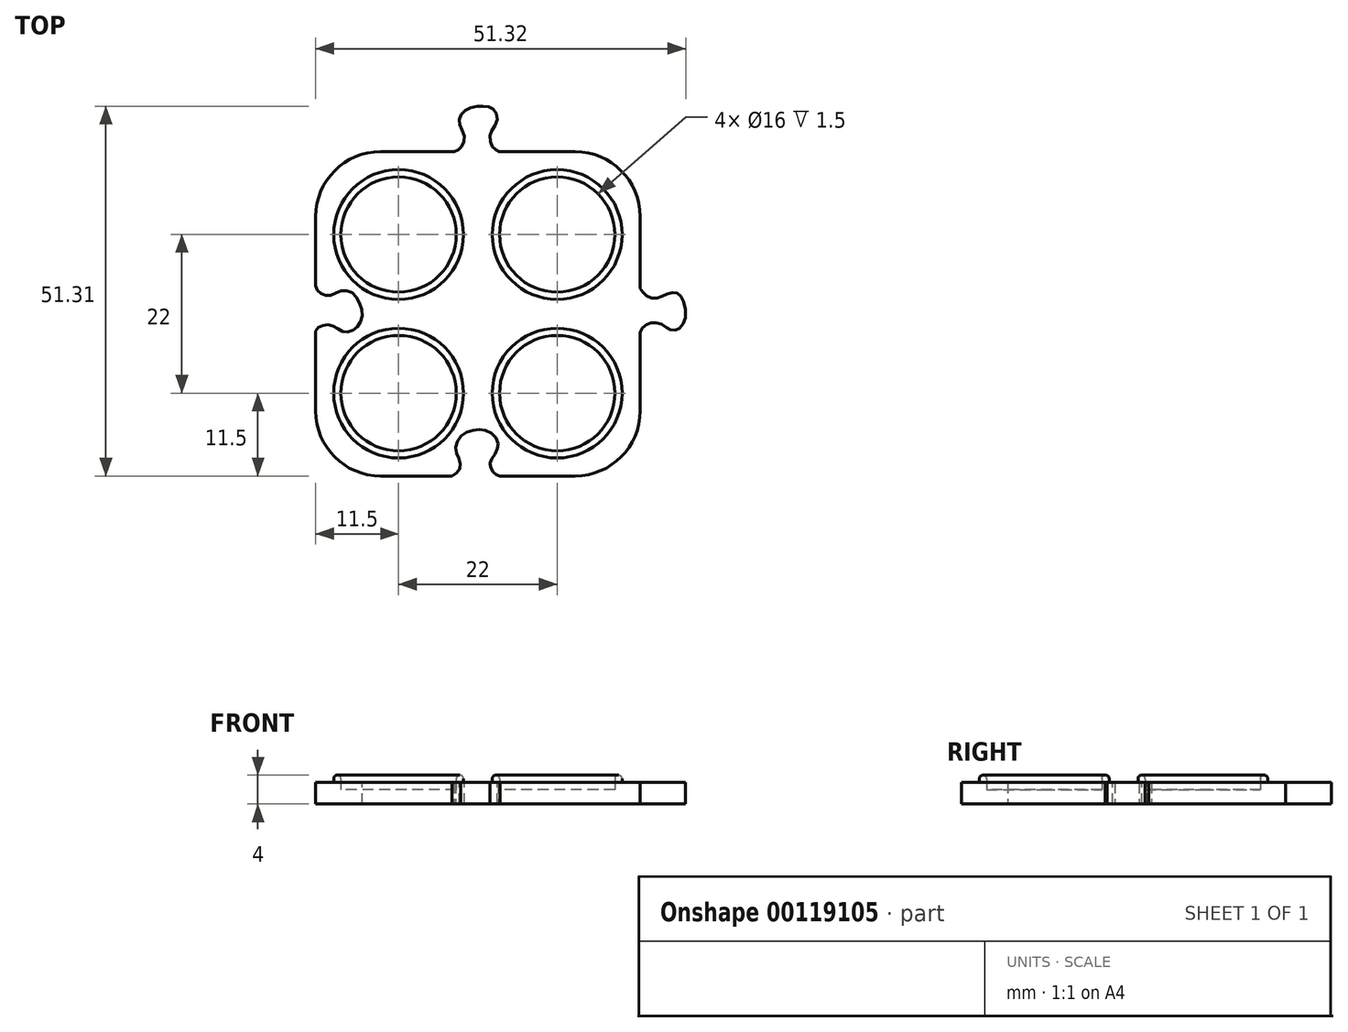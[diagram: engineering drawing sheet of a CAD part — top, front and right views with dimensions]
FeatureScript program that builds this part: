
annotation { "Feature Type Name" : "Feature", "Feature Type Description" : "" }
export const myFeature = defineFeature(function(context is Context, id is Id, definition is map)
    precondition{}
    {
        {
            var Q0;
            Q0=qCreatedBy(makeId("Top.planeOp"),FACE);
            var sketch = newSketch(context, id + "F0", { "sketchPlane" : qUnion([Q0])});
            skLineSegment(sketch, "E0.bottom", {"start": v(13.5, 13.5) * mm, "end": v(2.93, 13.5) * mm});
            skLineSegment(sketch, "E0.top", {"start": v(13.5, -13.5) * mm, "end": v(3.04, -13.5) * mm});
            skLineSegment(sketch, "E0.left", {"start": v(13.5, 13.5) * mm, "end": v(13.5, 3.49) * mm});
            skLineSegment(sketch, "E0.right", {"start": v(-13.5, 13.5) * mm, "end": v(-13.5, 3.89) * mm});
            skPoint(sketch, "E0.middle", {"position": v(0, 0) * mm});
            skFitSpline(sketch, "E1", {"points": [v(-13.5, -2.4) * mm, v(-13.06, -1.85) * mm, v(-12.19, -1.54) * mm, v(-11.23, -1.64) * mm, v(-10.18, -2.22) * mm, v(-9.3, -2.53) * mm, v(-8.23, -2.22) * mm, v(-7.52, -1.5) * mm, v(-7.03, -0.16) * mm, v(-7.37, 1.42) * mm, v(-8.21, 2.75) * mm, v(-9.3, 3.24) * mm, v(-10.53, 3) * mm, v(-11.5, 2.56) * mm, v(-12.42, 2.62) * mm, v(-13.18, 3.16) * mm, v(-13.5, 3.89) * mm], "startDerivative": vector(7.23, 11.93) * mm, "endDerivative": vector(-4.43, 14.21) * mm});
            skFitSpline(sketch, "E2", {"points": [v(-3.62, -13.5) * mm, v(-2.74, -12.9) * mm, v(-2.4, -12.05) * mm, v(-2.66, -11.08) * mm, v(-3.04, -10.02) * mm, v(-2.9, -8.8) * mm, v(-1.99, -7.67) * mm, v(-0.58, -7.14) * mm, v(0.76, -7.1) * mm, v(1.96, -7.62) * mm, v(2.79, -8.82) * mm, v(2.7, -9.8) * mm, v(2.12, -10.8) * mm, v(1.7, -11.65) * mm, v(1.76, -12.32) * mm, v(2.16, -13.02) * mm, v(2.6, -13.36) * mm, v(3.04, -13.5) * mm], "startDerivative": vector(16.2, 8.74) * mm, "endDerivative": vector(11.53, -2.8) * mm});
            skFitSpline(sketch, "E3", {"points": [v(-3.26, 13.5) * mm, v(-2.68, 13.76) * mm, v(-2.1, 14.46) * mm, v(-1.88, 15.61) * mm, v(-2.4, 17) * mm, v(-2.57, 17.9) * mm, v(-2.1, 18.93) * mm, v(-0.95, 19.6) * mm, v(0.43, 19.8) * mm, v(1.54, 19.7) * mm, v(2.37, 19.12) * mm, v(2.65, 17.8) * mm, v(2.02, 16.6) * mm, v(1.68, 15.55) * mm, v(1.92, 14.36) * mm, v(2.47, 13.75) * mm, v(2.93, 13.5) * mm], "startDerivative": vector(12.36, 4.01) * mm, "endDerivative": vector(10.48, -4.73) * mm});
            skFitSpline(sketch, "E4", {"points": [v(13.5, -2.57) * mm, v(13.97, -1.82) * mm, v(14.8, -1.34) * mm, v(15.69, -1.25) * mm, v(16.88, -1.66) * mm, v(17.63, -2.18) * mm, v(18.47, -2.24) * mm, v(19.2, -1.75) * mm, v(19.8, -0.34) * mm, v(19.4, 1.93) * mm, v(18.82, 2.75) * mm, v(18.04, 2.97) * mm, v(16.92, 2.58) * mm, v(15.97, 2.23) * mm, v(14.85, 2.24) * mm, v(13.98, 2.93) * mm, v(13.5, 3.49) * mm], "startDerivative": vector(6.76, 14.24) * mm, "endDerivative": vector(-8.43, 10.21) * mm});
            skLineSegment(sketch, "E5.trimOffspring", {"start": v(-3.26, 13.5) * mm, "end": v(-13.5, 13.5) * mm});
            skLineSegment(sketch, "E6.trimOffspring", {"start": v(13.5, -2.57) * mm, "end": v(13.5, -13.5) * mm});
            skLineSegment(sketch, "E7.trimOffspring", {"start": v(-3.62, -13.5) * mm, "end": v(-13.5, -13.5) * mm});
            skLineSegment(sketch, "E8.trimOffspring", {"start": v(-13.5, -2.4) * mm, "end": v(-13.5, -13.5) * mm});
            skPoint(sketch, "E9.visualSharp", {"position": v(-13.5, 13.5) * mm});
            skLineSegment(sketch, "E9.filletArc", {"start": v(-13.5, 13.5) * mm, "end": v(-13.5, 13.5) * mm});
            skPoint(sketch, "E10.visualSharp", {"position": v(13.5, 13.5) * mm});
            skLineSegment(sketch, "E10.filletArc", {"start": v(13.5, 13.5) * mm, "end": v(13.5, 13.5) * mm});
            skPoint(sketch, "E11.visualSharp", {"position": v(13.5, -13.5) * mm});
            skLineSegment(sketch, "E11.filletArc", {"start": v(13.5, -13.5) * mm, "end": v(13.5, -13.5) * mm});
            skPoint(sketch, "E12.visualSharp", {"position": v(-13.5, -13.5) * mm});
            skLineSegment(sketch, "E12.filletArc", {"start": v(-13.5, -13.5) * mm, "end": v(-13.5, -13.5) * mm});
            skLineSegment(sketch, "E13", {"start": v(-13.5, 4.5) * mm, "end": v(13.5, 4.5) * mm});
            skLineSegment(sketch, "E14", {"start": v(-4.5, 13.5) * mm, "end": v(-4.5, -13.5) * mm});
            skLineSegment(sketch, "E15", {"start": v(-13.5, -4.5) * mm, "end": v(13.5, -4.5) * mm});
            skLineSegment(sketch, "E16", {"start": v(4.5, 13.5) * mm, "end": v(4.5, -13.5) * mm});
            skSolve(sketch);
        }
        {
            var Q0;
            {var subQ1=sQuery(id+"F0.wireOp",EDGE,"E3");Q0=makeQuery(id+"F0.imprint","IMPRINT",FACE,{"disambiguationData":[TD([[makeQuery(id+"F0.imprint","IMPRINT",EDGE,{"derivedFrom":subQ1}),-1.0]])]});}
            var Q1;
            {var subQ0=sQuery(id+"F0.wireOp",EDGE,"E5.trimOffspring");var subQ1=sQuery(id+"F0.wireOp",EDGE,"E0.right");var subQ2=makeQuery(id+"F0.imprint","INTERSECT",VERTEX,{"derivedFrom":[subQ1,subQ0]});Q1=makeQuery(id+"F0.imprint","IMPRINT",FACE,{"disambiguationData":[TD([[makeQuery(id+"F0.imprint","IMPRINT",EDGE,{"disambiguationData":[TD([[subQ2,-1.0]])],"derivedFrom":subQ1}),1.0]])]});}
            var Q2;
            {var subQ0=sQuery(id+"F0.wireOp",EDGE,"E0.left");var subQ1=sQuery(id+"F0.wireOp",EDGE,"E0.bottom");var subQ2=makeQuery(id+"F0.imprint","INTERSECT",VERTEX,{"derivedFrom":[subQ1,subQ0]});Q2=makeQuery(id+"F0.imprint","IMPRINT",FACE,{"disambiguationData":[TD([[makeQuery(id+"F0.imprint","IMPRINT",EDGE,{"disambiguationData":[TD([[subQ2,-1.0]])],"derivedFrom":subQ1}),1.0]])]});}
            var Q3;
            {var subQ0=sQuery(id+"F0.wireOp",EDGE,"E14");var subQ1=sQuery(id+"F0.wireOp",EDGE,"E13");var subQ2=makeQuery(id+"F0.imprint","INTERSECT",VERTEX,{"derivedFrom":[subQ1,subQ0]});Q3=makeQuery(id+"F0.imprint","IMPRINT",FACE,{"disambiguationData":[TD([[makeQuery(id+"F0.imprint","IMPRINT",EDGE,{"disambiguationData":[TD([[subQ2,-1.0]])],"derivedFrom":subQ1}),-1.0]])]});}
            extrude(context, id + "F1", {"entities" : qUnion([Q0, Q1, Q2, Q3]), "depth" : 3 * mm});
        }
        {
            var Q0;
            {var subQ5=sQuery(id+"F0.wireOp",EDGE,"E4");Q0=makeQuery(id+"F0.imprint","IMPRINT",FACE,{"disambiguationData":[TD([[makeQuery(id+"F0.imprint","IMPRINT",EDGE,{"derivedFrom":subQ5}),1.0]])]});}
            var Q1;
            {var subQ0=sQuery(id+"F0.wireOp",EDGE,"E0.left");var subQ1=sQuery(id+"F0.wireOp",EDGE,"E0.bottom");var subQ2=makeQuery(id+"F0.imprint","INTERSECT",VERTEX,{"derivedFrom":[subQ1,subQ0]});Q1=makeQuery(id+"F0.imprint","IMPRINT",FACE,{"disambiguationData":[TD([[makeQuery(id+"F0.imprint","IMPRINT",EDGE,{"disambiguationData":[TD([[subQ2,-1.0]])],"derivedFrom":subQ1}),1.0]])]});}
            var Q2;
            {var subQ0=sQuery(id+"F0.wireOp",EDGE,"E6.trimOffspring");var subQ1=sQuery(id+"F0.wireOp",EDGE,"E0.top");var subQ2=makeQuery(id+"F0.imprint","INTERSECT",VERTEX,{"derivedFrom":[subQ1,subQ0]});Q2=makeQuery(id+"F0.imprint","IMPRINT",FACE,{"disambiguationData":[TD([[makeQuery(id+"F0.imprint","IMPRINT",EDGE,{"disambiguationData":[TD([[subQ2,-1.0]])],"derivedFrom":subQ1}),-1.0]])]});}
            var Q3;
            {var subQ0=sQuery(id+"F0.wireOp",EDGE,"E14");var subQ1=sQuery(id+"F0.wireOp",EDGE,"E13");var subQ2=makeQuery(id+"F0.imprint","INTERSECT",VERTEX,{"derivedFrom":[subQ1,subQ0]});Q3=makeQuery(id+"F0.imprint","IMPRINT",FACE,{"disambiguationData":[TD([[makeQuery(id+"F0.imprint","IMPRINT",EDGE,{"disambiguationData":[TD([[subQ2,-1.0]])],"derivedFrom":subQ1}),-1.0]])]});}
            extrude(context, id + "F2", {"entities" : qUnion([Q0, Q1, Q2, Q3]), "depth" : 3 * mm});
        }
        {
            var Q0;
            {var subQ5=sQuery(id+"F0.wireOp",EDGE,"E2");Q0=makeQuery(id+"F0.imprint","IMPRINT",FACE,{"disambiguationData":[TD([[makeQuery(id+"F0.imprint","IMPRINT",EDGE,{"derivedFrom":subQ5}),1.0]])]});}
            var Q1;
            {var subQ0=sQuery(id+"F0.wireOp",EDGE,"E8.trimOffspring");var subQ1=sQuery(id+"F0.wireOp",EDGE,"E7.trimOffspring");var subQ2=makeQuery(id+"F0.imprint","INTERSECT",VERTEX,{"derivedFrom":[subQ1,subQ0]});Q1=makeQuery(id+"F0.imprint","IMPRINT",FACE,{"disambiguationData":[TD([[makeQuery(id+"F0.imprint","IMPRINT",EDGE,{"disambiguationData":[TD([[subQ2,1.0]])],"derivedFrom":subQ1}),-1.0]])]});}
            var Q2;
            {var subQ0=sQuery(id+"F0.wireOp",EDGE,"E6.trimOffspring");var subQ1=sQuery(id+"F0.wireOp",EDGE,"E0.top");var subQ2=makeQuery(id+"F0.imprint","INTERSECT",VERTEX,{"derivedFrom":[subQ1,subQ0]});Q2=makeQuery(id+"F0.imprint","IMPRINT",FACE,{"disambiguationData":[TD([[makeQuery(id+"F0.imprint","IMPRINT",EDGE,{"disambiguationData":[TD([[subQ2,-1.0]])],"derivedFrom":subQ1}),-1.0]])]});}
            var Q3;
            {var subQ0=sQuery(id+"F0.wireOp",EDGE,"E14");var subQ1=sQuery(id+"F0.wireOp",EDGE,"E13");var subQ2=makeQuery(id+"F0.imprint","INTERSECT",VERTEX,{"derivedFrom":[subQ1,subQ0]});Q3=makeQuery(id+"F0.imprint","IMPRINT",FACE,{"disambiguationData":[TD([[makeQuery(id+"F0.imprint","IMPRINT",EDGE,{"disambiguationData":[TD([[subQ2,-1.0]])],"derivedFrom":subQ1}),-1.0]])]});}
            extrude(context, id + "F3", {"entities" : qUnion([Q0, Q1, Q2, Q3]), "depth" : 3 * mm});
        }
        {
            var Q0;
            {var subQ6=sQuery(id+"F0.wireOp",EDGE,"E1");Q0=makeQuery(id+"F0.imprint","IMPRINT",FACE,{"disambiguationData":[TD([[makeQuery(id+"F0.imprint","IMPRINT",EDGE,{"derivedFrom":subQ6}),-1.0]])]});}
            var Q1;
            {var subQ0=sQuery(id+"F0.wireOp",EDGE,"E5.trimOffspring");var subQ1=sQuery(id+"F0.wireOp",EDGE,"E0.right");var subQ2=makeQuery(id+"F0.imprint","INTERSECT",VERTEX,{"derivedFrom":[subQ1,subQ0]});Q1=makeQuery(id+"F0.imprint","IMPRINT",FACE,{"disambiguationData":[TD([[makeQuery(id+"F0.imprint","IMPRINT",EDGE,{"disambiguationData":[TD([[subQ2,-1.0]])],"derivedFrom":subQ1}),1.0]])]});}
            var Q2;
            {var subQ0=sQuery(id+"F0.wireOp",EDGE,"E8.trimOffspring");var subQ1=sQuery(id+"F0.wireOp",EDGE,"E7.trimOffspring");var subQ2=makeQuery(id+"F0.imprint","INTERSECT",VERTEX,{"derivedFrom":[subQ1,subQ0]});Q2=makeQuery(id+"F0.imprint","IMPRINT",FACE,{"disambiguationData":[TD([[makeQuery(id+"F0.imprint","IMPRINT",EDGE,{"disambiguationData":[TD([[subQ2,1.0]])],"derivedFrom":subQ1}),-1.0]])]});}
            var Q3;
            {var subQ0=sQuery(id+"F0.wireOp",EDGE,"E14");var subQ1=sQuery(id+"F0.wireOp",EDGE,"E13");var subQ2=makeQuery(id+"F0.imprint","INTERSECT",VERTEX,{"derivedFrom":[subQ1,subQ0]});Q3=makeQuery(id+"F0.imprint","IMPRINT",FACE,{"disambiguationData":[TD([[makeQuery(id+"F0.imprint","IMPRINT",EDGE,{"disambiguationData":[TD([[subQ2,-1.0]])],"derivedFrom":subQ1}),-1.0]])]});}
            extrude(context, id + "F4", {"entities" : qUnion([Q0, Q1, Q2, Q3]), "depth" : 3 * mm});
        }
        {
            var Q0;
            Q0=makeQuery(id+"F1.opExtrude","SWEPT_BODY",BODY,{"disambiguationData":[OSD([sQuery(id+"F0.wireOp",EDGE,"E0.bottom"),sQuery(id+"F0.wireOp",EDGE,"E0.left"),sQuery(id+"F0.wireOp",EDGE,"E0.right"),sQuery(id+"F0.wireOp",EDGE,"E3"),sQuery(id+"F0.wireOp",EDGE,"E5.trimOffspring"),sQuery(id+"F0.wireOp",EDGE,"E13"),sQuery(id+"F0.wireOp",EDGE,"E14"),sQuery(id+"F0.wireOp",EDGE,"E15"),sQuery(id+"F0.wireOp",EDGE,"E16")])]});
            transform(context, id + "F5", {"entities" : qUnion([Q0]), "transformType" : TransformType.TRANSLATION_3D, "dx" : 0 * mm, "dy" : 9 * mm, "dz" : 0 * mm, "makeCopy" : false});
        }
        {
            var Q0;
            Q0=makeQuery(id+"F2.opExtrude","SWEPT_BODY",BODY,{"disambiguationData":[OSD([sQuery(id+"F0.wireOp",EDGE,"E0.bottom"),sQuery(id+"F0.wireOp",EDGE,"E0.top"),sQuery(id+"F0.wireOp",EDGE,"E0.left"),sQuery(id+"F0.wireOp",EDGE,"E4"),sQuery(id+"F0.wireOp",EDGE,"E6.trimOffspring"),sQuery(id+"F0.wireOp",EDGE,"E13"),sQuery(id+"F0.wireOp",EDGE,"E14"),sQuery(id+"F0.wireOp",EDGE,"E15"),sQuery(id+"F0.wireOp",EDGE,"E16")])]});
            transform(context, id + "F6", {"entities" : qUnion([Q0]), "transformType" : TransformType.TRANSLATION_3D, "dx" : 9 * mm, "dy" : 0 * mm, "dz" : 0 * mm, "makeCopy" : false});
        }
        {
            var Q0;
            Q0=makeQuery(id+"F3.opExtrude","SWEPT_BODY",BODY,{"disambiguationData":[OSD([sQuery(id+"F0.wireOp",EDGE,"E0.top"),sQuery(id+"F0.wireOp",EDGE,"E2"),sQuery(id+"F0.wireOp",EDGE,"E6.trimOffspring"),sQuery(id+"F0.wireOp",EDGE,"E7.trimOffspring"),sQuery(id+"F0.wireOp",EDGE,"E8.trimOffspring"),sQuery(id+"F0.wireOp",EDGE,"E13"),sQuery(id+"F0.wireOp",EDGE,"E14"),sQuery(id+"F0.wireOp",EDGE,"E15"),sQuery(id+"F0.wireOp",EDGE,"E16")])]});
            transform(context, id + "F7", {"entities" : qUnion([Q0]), "transformType" : TransformType.TRANSLATION_3D, "dx" : 0 * mm, "dy" : -9 * mm, "dz" : 0 * mm, "makeCopy" : false});
        }
        {
            var Q0;
            Q0=makeQuery(id+"F4.opExtrude","SWEPT_BODY",BODY,{"disambiguationData":[OSD([sQuery(id+"F0.wireOp",EDGE,"E0.right"),sQuery(id+"F0.wireOp",EDGE,"E1"),sQuery(id+"F0.wireOp",EDGE,"E5.trimOffspring"),sQuery(id+"F0.wireOp",EDGE,"E7.trimOffspring"),sQuery(id+"F0.wireOp",EDGE,"E8.trimOffspring"),sQuery(id+"F0.wireOp",EDGE,"E13"),sQuery(id+"F0.wireOp",EDGE,"E14"),sQuery(id+"F0.wireOp",EDGE,"E15"),sQuery(id+"F0.wireOp",EDGE,"E16")])]});
            transform(context, id + "F8", {"entities" : qUnion([Q0]), "transformType" : TransformType.TRANSLATION_3D, "dx" : -9 * mm, "dy" : 0 * mm, "dz" : 0 * mm, "makeCopy" : false});
        }
        {
            var Q0;
            Q0=qCreatedBy(makeId("Top.planeOp"),FACE);
            var sketch = newSketch(context, id + "F9", { "sketchPlane" : qUnion([Q0])});
            skLineSegment(sketch, "E17.top", {"start": v(13.5, 22.5) * mm, "end": v(-13.5, 22.5) * mm});
            skLineSegment(sketch, "E17.left", {"start": v(22.5, -13.5) * mm, "end": v(22.5, 13.5) * mm});
            skPoint(sketch, "E18.visualSharp", {"position": v(22.5, 22.5) * mm});
            skArc(sketch, "E18.filletArc", {"start": v(22.5, 13.5) * mm, "mid": v(19.86, 19.86) * mm, "end": v(13.5, 22.5) * mm});
            skPoint(sketch, "E19.visualSharp", {"position": v(22.5, -22.5) * mm});
            skArc(sketch, "E19.filletArc", {"start": v(13.5, -22.5) * mm, "mid": v(19.86, -19.86) * mm, "end": v(22.5, -13.5) * mm});
            skPoint(sketch, "E20.visualSharp", {"position": v(-22.5, -22.5) * mm});
            skArc(sketch, "E20.filletArc", {"start": v(-22.5, -13.5) * mm, "mid": v(-19.86, -19.86) * mm, "end": v(-13.5, -22.5) * mm});
            skPoint(sketch, "E21.visualSharp", {"position": v(-22.5, 22.5) * mm});
            skArc(sketch, "E21.filletArc", {"start": v(-13.5, 22.5) * mm, "mid": v(-19.86, 19.86) * mm, "end": v(-22.5, 13.5) * mm});
            skLineSegment(sketch, "E22", {"start": v(-22.5, 13.5) * mm, "end": v(-12.08, 0) * mm});
            skLineSegment(sketch, "E23", {"start": v(-12.08, 0) * mm, "end": v(-22.5, -13.5) * mm});
            skLineSegment(sketch, "E24", {"start": v(-13.5, -22.5) * mm, "end": v(0, -11.74) * mm});
            skLineSegment(sketch, "E25", {"start": v(13.5, -22.5) * mm, "end": v(0, -11.74) * mm});
            skSolve(sketch);
        }
        {
            var Q0;
            Q0 = qSketchRegion(id + "F9", true);
            extrude(context, id + "F10", {"entities" : qUnion([Q0]), "depth" : 3 * mm});
        }
        {
            var Q0;
            Q0=makeQuery(id+"F1.opExtrude","SWEPT_BODY",BODY,{"disambiguationData":[OSD([sQuery(id+"F0.wireOp",EDGE,"E0.bottom"),sQuery(id+"F0.wireOp",EDGE,"E0.left"),sQuery(id+"F0.wireOp",EDGE,"E0.right"),sQuery(id+"F0.wireOp",EDGE,"E3"),sQuery(id+"F0.wireOp",EDGE,"E5.trimOffspring"),sQuery(id+"F0.wireOp",EDGE,"E13"),sQuery(id+"F0.wireOp",EDGE,"E14"),sQuery(id+"F0.wireOp",EDGE,"E15"),sQuery(id+"F0.wireOp",EDGE,"E16")])]});
            var Q1;
            Q1=makeQuery(id+"F2.opExtrude","SWEPT_BODY",BODY,{"disambiguationData":[OSD([sQuery(id+"F0.wireOp",EDGE,"E0.bottom"),sQuery(id+"F0.wireOp",EDGE,"E0.top"),sQuery(id+"F0.wireOp",EDGE,"E0.left"),sQuery(id+"F0.wireOp",EDGE,"E4"),sQuery(id+"F0.wireOp",EDGE,"E6.trimOffspring"),sQuery(id+"F0.wireOp",EDGE,"E13"),sQuery(id+"F0.wireOp",EDGE,"E14"),sQuery(id+"F0.wireOp",EDGE,"E15"),sQuery(id+"F0.wireOp",EDGE,"E16")])]});
            var Q2;
            Q2=makeQuery(id+"F3.opExtrude","SWEPT_BODY",BODY,{"disambiguationData":[OSD([sQuery(id+"F0.wireOp",EDGE,"E0.top"),sQuery(id+"F0.wireOp",EDGE,"E2"),sQuery(id+"F0.wireOp",EDGE,"E6.trimOffspring"),sQuery(id+"F0.wireOp",EDGE,"E7.trimOffspring"),sQuery(id+"F0.wireOp",EDGE,"E8.trimOffspring"),sQuery(id+"F0.wireOp",EDGE,"E13"),sQuery(id+"F0.wireOp",EDGE,"E14"),sQuery(id+"F0.wireOp",EDGE,"E15"),sQuery(id+"F0.wireOp",EDGE,"E16")])]});
            var Q3;
            Q3=makeQuery(id+"F4.opExtrude","SWEPT_BODY",BODY,{"disambiguationData":[OSD([sQuery(id+"F0.wireOp",EDGE,"E0.right"),sQuery(id+"F0.wireOp",EDGE,"E1"),sQuery(id+"F0.wireOp",EDGE,"E5.trimOffspring"),sQuery(id+"F0.wireOp",EDGE,"E7.trimOffspring"),sQuery(id+"F0.wireOp",EDGE,"E8.trimOffspring"),sQuery(id+"F0.wireOp",EDGE,"E13"),sQuery(id+"F0.wireOp",EDGE,"E14"),sQuery(id+"F0.wireOp",EDGE,"E15"),sQuery(id+"F0.wireOp",EDGE,"E16")])]});
            var Q4;
            Q4=makeQuery(id+"F10.opExtrude","SWEPT_BODY",BODY,{"disambiguationData":[OSD([sQuery(id+"F9.wireOp",EDGE,"E17.top"),sQuery(id+"F9.wireOp",EDGE,"E17.left"),sQuery(id+"F9.wireOp",EDGE,"E18.filletArc"),sQuery(id+"F9.wireOp",EDGE,"E19.filletArc"),sQuery(id+"F9.wireOp",EDGE,"E20.filletArc"),sQuery(id+"F9.wireOp",EDGE,"E21.filletArc"),sQuery(id+"F9.wireOp",EDGE,"E22"),sQuery(id+"F9.wireOp",EDGE,"E23"),sQuery(id+"F9.wireOp",EDGE,"E24"),sQuery(id+"F9.wireOp",EDGE,"E25")])]});
            booleanBodies(context, id + "F11", {"operationType" : BooleanOperationType.UNION, "tools" : qUnion([Q0, Q1, Q2, Q3, Q4])});
        }
        {
            var Q0;
            {var subQ0=sQuery(id+"F0.wireOp",EDGE,"E16");var subQ1=sQuery(id+"F0.wireOp",EDGE,"E15");var subQ2=sQuery(id+"F0.wireOp",EDGE,"E14");var subQ3=sQuery(id+"F0.wireOp",EDGE,"E13");var subQ4=sQuery(id+"F0.wireOp",EDGE,"E8.trimOffspring");var subQ5=sQuery(id+"F0.wireOp",EDGE,"E7.trimOffspring");var subQ6=sQuery(id+"F0.wireOp",EDGE,"E5.trimOffspring");var subQ7=sQuery(id+"F0.wireOp",EDGE,"E0.right");var subQ8=sQuery(id+"F0.wireOp",EDGE,"E6.trimOffspring");var subQ9=sQuery(id+"F0.wireOp",EDGE,"E0.top");var subQ10=sQuery(id+"F0.wireOp",EDGE,"E0.left");var subQ11=sQuery(id+"F0.wireOp",EDGE,"E0.bottom");Q0=makeQuery(id+"F11.opBoolean","MERGE",FACE,{"derivedFrom":[makeQuery(id+"F1.opExtrude","CAP_FACE",FACE,{"disambiguationData":[OSD([subQ11,subQ10,subQ7,sQuery(id+"F0.wireOp",EDGE,"E3"),subQ6,subQ3,subQ2,subQ1,subQ0])],"isStart":false}),makeQuery(id+"F2.opExtrude","CAP_FACE",FACE,{"disambiguationData":[OSD([subQ11,subQ9,subQ10,sQuery(id+"F0.wireOp",EDGE,"E4"),subQ8,subQ3,subQ2,subQ1,subQ0])],"isStart":false}),makeQuery(id+"F3.opExtrude","CAP_FACE",FACE,{"disambiguationData":[OSD([subQ9,sQuery(id+"F0.wireOp",EDGE,"E2"),subQ8,subQ5,subQ4,subQ3,subQ2,subQ1,subQ0])],"isStart":false}),makeQuery(id+"F4.opExtrude","CAP_FACE",FACE,{"disambiguationData":[OSD([subQ7,sQuery(id+"F0.wireOp",EDGE,"E1"),subQ6,subQ5,subQ4,subQ3,subQ2,subQ1,subQ0])],"isStart":false}),makeQuery(id+"F10.opExtrude","CAP_FACE",FACE,{"disambiguationData":[OSD([sQuery(id+"F9.wireOp",EDGE,"E17.top"),sQuery(id+"F9.wireOp",EDGE,"E17.left"),sQuery(id+"F9.wireOp",EDGE,"E18.filletArc"),sQuery(id+"F9.wireOp",EDGE,"E19.filletArc"),sQuery(id+"F9.wireOp",EDGE,"E20.filletArc"),sQuery(id+"F9.wireOp",EDGE,"E21.filletArc"),sQuery(id+"F9.wireOp",EDGE,"E22"),sQuery(id+"F9.wireOp",EDGE,"E23"),sQuery(id+"F9.wireOp",EDGE,"E24"),sQuery(id+"F9.wireOp",EDGE,"E25")])],"isStart":false})]});}
            var sketch = newSketch(context, id + "F12", { "sketchPlane" : qUnion([Q0])});
            skLineSegment(sketch, "E26.bottom", {"start": v(11, -11) * mm, "end": v(-11, -11) * mm, "construction": true});
            skLineSegment(sketch, "E26.top", {"start": v(11, 11) * mm, "end": v(-11, 11) * mm, "construction": true});
            skLineSegment(sketch, "E26.left", {"start": v(11, -11) * mm, "end": v(11, 11) * mm, "construction": true});
            skLineSegment(sketch, "E26.right", {"start": v(-11, -11) * mm, "end": v(-11, 11) * mm, "construction": true});
            skPoint(sketch, "E26.middle", {"position": v(0, 0) * mm});
            skCircle(sketch, "E27", {"center": v(-11, 11) * mm, "radius": 9 * mm});
            skCircle(sketch, "E28", {"center": v(11, 11) * mm, "radius": 9 * mm});
            skCircle(sketch, "E29", {"center": v(11, -11) * mm, "radius": 9 * mm});
            skCircle(sketch, "E30", {"center": v(-11, -11) * mm, "radius": 9 * mm});
            skCircle(sketch, "E31", {"center": v(-11, 11) * mm, "radius": 8 * mm});
            skCircle(sketch, "E32", {"center": v(11, 11) * mm, "radius": 8 * mm});
            skCircle(sketch, "E33", {"center": v(11, -11) * mm, "radius": 8 * mm});
            skCircle(sketch, "E34", {"center": v(-11, -11) * mm, "radius": 8 * mm});
            skSolve(sketch);
        }
        {
            var Q0;
            Q0=makeQuery(id+"F12.imprint","IMPRINT",FACE,{"disambiguationData":[TD([[makeQuery(id+"F12.imprint","IMPRINT",EDGE,{"derivedFrom":sQuery(id+"F12.wireOp",EDGE,"E27")}),1.0]])]});
            var Q1;
            Q1=makeQuery(id+"F12.imprint","IMPRINT",FACE,{"disambiguationData":[TD([[makeQuery(id+"F12.imprint","IMPRINT",EDGE,{"derivedFrom":sQuery(id+"F12.wireOp",EDGE,"E28")}),1.0]])]});
            var Q2;
            Q2=makeQuery(id+"F12.imprint","IMPRINT",FACE,{"disambiguationData":[TD([[makeQuery(id+"F12.imprint","IMPRINT",EDGE,{"derivedFrom":sQuery(id+"F12.wireOp",EDGE,"E29")}),1.0]])]});
            var Q3;
            Q3=makeQuery(id+"F12.imprint","IMPRINT",FACE,{"disambiguationData":[TD([[makeQuery(id+"F12.imprint","IMPRINT",EDGE,{"derivedFrom":sQuery(id+"F12.wireOp",EDGE,"E30")}),1.0]])]});
            extrude(context, id + "F13", {"entities" : qUnion([Q0, Q1, Q2, Q3]), "operationType" : NewBodyOperationType.ADD, "depth" : 1 * mm});
        }
        {
            var Q0;
            {var subQ0=sQuery(id+"F0.wireOp",EDGE,"E16");var subQ1=sQuery(id+"F0.wireOp",EDGE,"E15");var subQ2=sQuery(id+"F0.wireOp",EDGE,"E14");var subQ3=sQuery(id+"F0.wireOp",EDGE,"E13");var subQ4=sQuery(id+"F0.wireOp",EDGE,"E8.trimOffspring");var subQ5=sQuery(id+"F0.wireOp",EDGE,"E7.trimOffspring");var subQ6=sQuery(id+"F0.wireOp",EDGE,"E5.trimOffspring");var subQ7=sQuery(id+"F0.wireOp",EDGE,"E0.right");var subQ8=sQuery(id+"F0.wireOp",EDGE,"E6.trimOffspring");var subQ9=sQuery(id+"F0.wireOp",EDGE,"E0.top");var subQ10=sQuery(id+"F0.wireOp",EDGE,"E0.left");var subQ11=sQuery(id+"F0.wireOp",EDGE,"E0.bottom");Q0=makeQuery(id+"F13.boolean.opBoolean","SPLIT",FACE,{"disambiguationData":[TD([makeQuery(id+"F13.opExtrude","SWEPT_FACE",FACE,{"disambiguationData":[OSD([sQuery(id+"F12.wireOp",EDGE,"E34")])]})])],"derivedFrom":makeQuery(id+"F11.opBoolean","MERGE",FACE,{"derivedFrom":[makeQuery(id+"F1.opExtrude","CAP_FACE",FACE,{"disambiguationData":[OSD([subQ11,subQ10,subQ7,sQuery(id+"F0.wireOp",EDGE,"E3"),subQ6,subQ3,subQ2,subQ1,subQ0])],"isStart":false}),makeQuery(id+"F2.opExtrude","CAP_FACE",FACE,{"disambiguationData":[OSD([subQ11,subQ9,subQ10,sQuery(id+"F0.wireOp",EDGE,"E4"),subQ8,subQ3,subQ2,subQ1,subQ0])],"isStart":false}),makeQuery(id+"F3.opExtrude","CAP_FACE",FACE,{"disambiguationData":[OSD([subQ9,sQuery(id+"F0.wireOp",EDGE,"E2"),subQ8,subQ5,subQ4,subQ3,subQ2,subQ1,subQ0])],"isStart":false}),makeQuery(id+"F4.opExtrude","CAP_FACE",FACE,{"disambiguationData":[OSD([subQ7,sQuery(id+"F0.wireOp",EDGE,"E1"),subQ6,subQ5,subQ4,subQ3,subQ2,subQ1,subQ0])],"isStart":false}),makeQuery(id+"F10.opExtrude","CAP_FACE",FACE,{"disambiguationData":[OSD([sQuery(id+"F9.wireOp",EDGE,"E17.top"),sQuery(id+"F9.wireOp",EDGE,"E17.left"),sQuery(id+"F9.wireOp",EDGE,"E18.filletArc"),sQuery(id+"F9.wireOp",EDGE,"E19.filletArc"),sQuery(id+"F9.wireOp",EDGE,"E20.filletArc"),sQuery(id+"F9.wireOp",EDGE,"E21.filletArc"),sQuery(id+"F9.wireOp",EDGE,"E22"),sQuery(id+"F9.wireOp",EDGE,"E23"),sQuery(id+"F9.wireOp",EDGE,"E24"),sQuery(id+"F9.wireOp",EDGE,"E25")])],"isStart":false})]})});}
            var Q1;
            {var subQ0=sQuery(id+"F0.wireOp",EDGE,"E16");var subQ1=sQuery(id+"F0.wireOp",EDGE,"E15");var subQ2=sQuery(id+"F0.wireOp",EDGE,"E14");var subQ3=sQuery(id+"F0.wireOp",EDGE,"E13");var subQ4=sQuery(id+"F0.wireOp",EDGE,"E8.trimOffspring");var subQ5=sQuery(id+"F0.wireOp",EDGE,"E7.trimOffspring");var subQ6=sQuery(id+"F0.wireOp",EDGE,"E5.trimOffspring");var subQ7=sQuery(id+"F0.wireOp",EDGE,"E0.right");var subQ8=sQuery(id+"F0.wireOp",EDGE,"E6.trimOffspring");var subQ9=sQuery(id+"F0.wireOp",EDGE,"E0.top");var subQ10=sQuery(id+"F0.wireOp",EDGE,"E0.left");var subQ11=sQuery(id+"F0.wireOp",EDGE,"E0.bottom");Q1=makeQuery(id+"F13.boolean.opBoolean","SPLIT",FACE,{"disambiguationData":[TD([makeQuery(id+"F13.opExtrude","SWEPT_FACE",FACE,{"disambiguationData":[OSD([sQuery(id+"F12.wireOp",EDGE,"E31")])]})])],"derivedFrom":makeQuery(id+"F11.opBoolean","MERGE",FACE,{"derivedFrom":[makeQuery(id+"F1.opExtrude","CAP_FACE",FACE,{"disambiguationData":[OSD([subQ11,subQ10,subQ7,sQuery(id+"F0.wireOp",EDGE,"E3"),subQ6,subQ3,subQ2,subQ1,subQ0])],"isStart":false}),makeQuery(id+"F2.opExtrude","CAP_FACE",FACE,{"disambiguationData":[OSD([subQ11,subQ9,subQ10,sQuery(id+"F0.wireOp",EDGE,"E4"),subQ8,subQ3,subQ2,subQ1,subQ0])],"isStart":false}),makeQuery(id+"F3.opExtrude","CAP_FACE",FACE,{"disambiguationData":[OSD([subQ9,sQuery(id+"F0.wireOp",EDGE,"E2"),subQ8,subQ5,subQ4,subQ3,subQ2,subQ1,subQ0])],"isStart":false}),makeQuery(id+"F4.opExtrude","CAP_FACE",FACE,{"disambiguationData":[OSD([subQ7,sQuery(id+"F0.wireOp",EDGE,"E1"),subQ6,subQ5,subQ4,subQ3,subQ2,subQ1,subQ0])],"isStart":false}),makeQuery(id+"F10.opExtrude","CAP_FACE",FACE,{"disambiguationData":[OSD([sQuery(id+"F9.wireOp",EDGE,"E17.top"),sQuery(id+"F9.wireOp",EDGE,"E17.left"),sQuery(id+"F9.wireOp",EDGE,"E18.filletArc"),sQuery(id+"F9.wireOp",EDGE,"E19.filletArc"),sQuery(id+"F9.wireOp",EDGE,"E20.filletArc"),sQuery(id+"F9.wireOp",EDGE,"E21.filletArc"),sQuery(id+"F9.wireOp",EDGE,"E22"),sQuery(id+"F9.wireOp",EDGE,"E23"),sQuery(id+"F9.wireOp",EDGE,"E24"),sQuery(id+"F9.wireOp",EDGE,"E25")])],"isStart":false})]})});}
            var Q2;
            {var subQ0=sQuery(id+"F0.wireOp",EDGE,"E16");var subQ1=sQuery(id+"F0.wireOp",EDGE,"E15");var subQ2=sQuery(id+"F0.wireOp",EDGE,"E14");var subQ3=sQuery(id+"F0.wireOp",EDGE,"E13");var subQ4=sQuery(id+"F0.wireOp",EDGE,"E8.trimOffspring");var subQ5=sQuery(id+"F0.wireOp",EDGE,"E7.trimOffspring");var subQ6=sQuery(id+"F0.wireOp",EDGE,"E5.trimOffspring");var subQ7=sQuery(id+"F0.wireOp",EDGE,"E0.right");var subQ8=sQuery(id+"F0.wireOp",EDGE,"E6.trimOffspring");var subQ9=sQuery(id+"F0.wireOp",EDGE,"E0.top");var subQ10=sQuery(id+"F0.wireOp",EDGE,"E0.left");var subQ11=sQuery(id+"F0.wireOp",EDGE,"E0.bottom");Q2=makeQuery(id+"F13.boolean.opBoolean","SPLIT",FACE,{"disambiguationData":[TD([makeQuery(id+"F13.opExtrude","SWEPT_FACE",FACE,{"disambiguationData":[OSD([sQuery(id+"F12.wireOp",EDGE,"E32")])]})])],"derivedFrom":makeQuery(id+"F11.opBoolean","MERGE",FACE,{"derivedFrom":[makeQuery(id+"F1.opExtrude","CAP_FACE",FACE,{"disambiguationData":[OSD([subQ11,subQ10,subQ7,sQuery(id+"F0.wireOp",EDGE,"E3"),subQ6,subQ3,subQ2,subQ1,subQ0])],"isStart":false}),makeQuery(id+"F2.opExtrude","CAP_FACE",FACE,{"disambiguationData":[OSD([subQ11,subQ9,subQ10,sQuery(id+"F0.wireOp",EDGE,"E4"),subQ8,subQ3,subQ2,subQ1,subQ0])],"isStart":false}),makeQuery(id+"F3.opExtrude","CAP_FACE",FACE,{"disambiguationData":[OSD([subQ9,sQuery(id+"F0.wireOp",EDGE,"E2"),subQ8,subQ5,subQ4,subQ3,subQ2,subQ1,subQ0])],"isStart":false}),makeQuery(id+"F4.opExtrude","CAP_FACE",FACE,{"disambiguationData":[OSD([subQ7,sQuery(id+"F0.wireOp",EDGE,"E1"),subQ6,subQ5,subQ4,subQ3,subQ2,subQ1,subQ0])],"isStart":false}),makeQuery(id+"F10.opExtrude","CAP_FACE",FACE,{"disambiguationData":[OSD([sQuery(id+"F9.wireOp",EDGE,"E17.top"),sQuery(id+"F9.wireOp",EDGE,"E17.left"),sQuery(id+"F9.wireOp",EDGE,"E18.filletArc"),sQuery(id+"F9.wireOp",EDGE,"E19.filletArc"),sQuery(id+"F9.wireOp",EDGE,"E20.filletArc"),sQuery(id+"F9.wireOp",EDGE,"E21.filletArc"),sQuery(id+"F9.wireOp",EDGE,"E22"),sQuery(id+"F9.wireOp",EDGE,"E23"),sQuery(id+"F9.wireOp",EDGE,"E24"),sQuery(id+"F9.wireOp",EDGE,"E25")])],"isStart":false})]})});}
            var Q3;
            {var subQ0=sQuery(id+"F0.wireOp",EDGE,"E16");var subQ1=sQuery(id+"F0.wireOp",EDGE,"E15");var subQ2=sQuery(id+"F0.wireOp",EDGE,"E14");var subQ3=sQuery(id+"F0.wireOp",EDGE,"E13");var subQ4=sQuery(id+"F0.wireOp",EDGE,"E8.trimOffspring");var subQ5=sQuery(id+"F0.wireOp",EDGE,"E7.trimOffspring");var subQ6=sQuery(id+"F0.wireOp",EDGE,"E5.trimOffspring");var subQ7=sQuery(id+"F0.wireOp",EDGE,"E0.right");var subQ8=sQuery(id+"F0.wireOp",EDGE,"E6.trimOffspring");var subQ9=sQuery(id+"F0.wireOp",EDGE,"E0.top");var subQ10=sQuery(id+"F0.wireOp",EDGE,"E0.left");var subQ11=sQuery(id+"F0.wireOp",EDGE,"E0.bottom");Q3=makeQuery(id+"F13.boolean.opBoolean","SPLIT",FACE,{"disambiguationData":[TD([makeQuery(id+"F13.opExtrude","SWEPT_FACE",FACE,{"disambiguationData":[OSD([sQuery(id+"F12.wireOp",EDGE,"E33")])]})])],"derivedFrom":makeQuery(id+"F11.opBoolean","MERGE",FACE,{"derivedFrom":[makeQuery(id+"F1.opExtrude","CAP_FACE",FACE,{"disambiguationData":[OSD([subQ11,subQ10,subQ7,sQuery(id+"F0.wireOp",EDGE,"E3"),subQ6,subQ3,subQ2,subQ1,subQ0])],"isStart":false}),makeQuery(id+"F2.opExtrude","CAP_FACE",FACE,{"disambiguationData":[OSD([subQ11,subQ9,subQ10,sQuery(id+"F0.wireOp",EDGE,"E4"),subQ8,subQ3,subQ2,subQ1,subQ0])],"isStart":false}),makeQuery(id+"F3.opExtrude","CAP_FACE",FACE,{"disambiguationData":[OSD([subQ9,sQuery(id+"F0.wireOp",EDGE,"E2"),subQ8,subQ5,subQ4,subQ3,subQ2,subQ1,subQ0])],"isStart":false}),makeQuery(id+"F4.opExtrude","CAP_FACE",FACE,{"disambiguationData":[OSD([subQ7,sQuery(id+"F0.wireOp",EDGE,"E1"),subQ6,subQ5,subQ4,subQ3,subQ2,subQ1,subQ0])],"isStart":false}),makeQuery(id+"F10.opExtrude","CAP_FACE",FACE,{"disambiguationData":[OSD([sQuery(id+"F9.wireOp",EDGE,"E17.top"),sQuery(id+"F9.wireOp",EDGE,"E17.left"),sQuery(id+"F9.wireOp",EDGE,"E18.filletArc"),sQuery(id+"F9.wireOp",EDGE,"E19.filletArc"),sQuery(id+"F9.wireOp",EDGE,"E20.filletArc"),sQuery(id+"F9.wireOp",EDGE,"E21.filletArc"),sQuery(id+"F9.wireOp",EDGE,"E22"),sQuery(id+"F9.wireOp",EDGE,"E23"),sQuery(id+"F9.wireOp",EDGE,"E24"),sQuery(id+"F9.wireOp",EDGE,"E25")])],"isStart":false})]})});}
            extrude(context, id + "F14", {"entities" : qUnion([Q0, Q1, Q2, Q3]), "operationType" : NewBodyOperationType.REMOVE, "depth" : -1 * mm});
        }
        {
            var Q0;
            Q0=makeQuery(id+"F13.opExtrude","CAP_FACE",FACE,{"disambiguationData":[OSD([sQuery(id+"F12.wireOp",EDGE,"E30"),sQuery(id+"F12.wireOp",EDGE,"E34")])],"isStart":false});
            fillet(context, id + "F15", {"entities" : qUnion([Q0]), "radius" : 0.5 * mm, "tangentPropagation" : true, "allowEdgeOverflow" : false});
        }
        {
            var Q0;
            Q0=makeQuery(id+"F13.opExtrude","CAP_FACE",FACE,{"disambiguationData":[OSD([sQuery(id+"F12.wireOp",EDGE,"E27"),sQuery(id+"F12.wireOp",EDGE,"E31")])],"isStart":false});
            fillet(context, id + "F16", {"entities" : qUnion([Q0]), "radius" : 0.5 * mm, "tangentPropagation" : true, "allowEdgeOverflow" : false});
        }
        {
            var Q0;
            Q0=makeQuery(id+"F13.opExtrude","CAP_FACE",FACE,{"disambiguationData":[OSD([sQuery(id+"F12.wireOp",EDGE,"E28"),sQuery(id+"F12.wireOp",EDGE,"E32")])],"isStart":false});
            fillet(context, id + "F17", {"entities" : qUnion([Q0]), "radius" : 0.5 * mm, "tangentPropagation" : true, "allowEdgeOverflow" : false});
        }
        {
            var Q0;
            Q0=makeQuery(id+"F13.opExtrude","CAP_FACE",FACE,{"disambiguationData":[OSD([sQuery(id+"F12.wireOp",EDGE,"E29"),sQuery(id+"F12.wireOp",EDGE,"E33")])],"isStart":false});
            fillet(context, id + "F18", {"entities" : qUnion([Q0]), "radius" : 0.5 * mm, "tangentPropagation" : true, "allowEdgeOverflow" : false});
        }
    });
